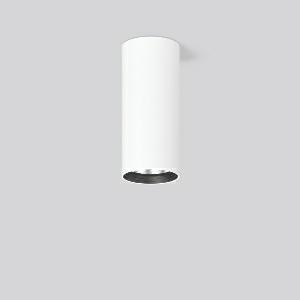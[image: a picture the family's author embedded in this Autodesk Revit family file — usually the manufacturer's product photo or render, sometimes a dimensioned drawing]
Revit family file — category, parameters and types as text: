
# Revit family: heledon_mini_a_931200_002_3_fbb7
name_source: partatom
category: Lighting Fixtures
units: mm (PartAtom-declared; Revit-internal decimal feet)

## family parameters
Cut with Voids When Loaded = No
Host = Face
Light Source = No
Part Type = Normal
Room Calculation Point = No
Round Connector Dimension = Use Diameter
Shared = No

## types (1)
- HELEDON mini A (1 x LED Modul 935, 2600 lm, 3500)
    Apparent Load = 20 VA
    Approval mark = CE
    CIE Flux Codes = 100 100 100 100 100
    Color Rendering = 92
    Color Temperature = 3500
    Default Elevation = 1800 mm
    Description = Series: HELEDON mini
Cylindrical surface-mounted downlight. Housing: die-cast aluminium, powder-coated. Internal ceiling frame polycarbonate with bayonet mounting. Black plastic ring and recessed LED to prevent glare from the side. Optical assembly with reflector made of MIRO-Silver with 98% total light reflection for outstanding efficiency - can be changed without tools. Best colour rendering index Ra>90. Suitable for Ceiling mounting. Easy installation with a separate ceiling frame with bayonet mounting and plug connection. Driver integrated. Connected via plug-in connector. High quality converter without flickering and stroboscopic effect. The following accessories can be mounted without use of tools: interchangeable lenses, decorative glasses, honeycomb louvre, clear and frosted diffusers, white interchangeable plastic ring. 
Colour: traffic white, matt (RAL 9016)
Diameter: 87 mm
Height: 197 mm
Lamp: LED
Socket: without socket
Colour temperature: 3500K
Colour rendering index (CRI): 92
System power: 20 W
Rated luminous flux: 2600 lm
Luminous efficiency: 130 lm/W
Control gear: Regulated power supply
Protection class: I
Type of protection: IP 20
    Height = 197 mm
    Lamp = 1 x LED Modul 935
    Lamp Light Flux = 2600 lm
    Lamp count = 1
    Length = 87 mm
    Lifetime = 50000 h
    Luminous efficacy = 130 lm/W
    Manufacturer = RZB
    ModVariant = No
    Model = 931200.002.3
    Mounting Place = Ceiling
    Mounting Type = Surface mounted
    Number of Poles = 1
    OnlyDefault = Yes
    Power Factor = 1
    Product Name = HELEDON mini A
    Product group = Surface mounted downlights
    ProductGroupID = 302
    Protection Class = Protection class I
    Protection Degree = IP 20
    RLX_Detail_Level = 1
    RLX_Emergency_Light_Flux = 0 lm
    RLX_Emergency_Type = 0
    RLX_Emergency_Type_DB = No
    RlxData = <blob elided: 107461 chars, md5=51abbea2>
    Socket = socket
    Standby Power = 0 W
    System Light Flux = 2600 lm
    System Power = 20 W
    Type Comments = Product without accessories
    Type Image = 931188.002.jpg
    URL = http://relux.com
    VarID = ---
    Voltage = 230 V
    Voltage Range = 220-240 V
    Weight = 0.00 kg
    Width = 0 mm  [stored 0 ft]

note: [stored X ft] marks values corroborated as IEEE doubles in the binary element streams (Revit-internal decimal feet)

## geometry (parser evidence)
native form markers: Blend x4, Sweep x11
no freeform markers — native parametric forms only
